# Revit family: Strangregulierventil mit Messblende für Trinkwasseranlagen 4017 MW
name_source: partatom
category: Rohrzubehör
units: mm (PartAtom-declared; Revit-internal decimal feet)

## family parameters
Arbeitsebenenbasiert = Nein
Beim Laden mit Abzugskörper schneiden = Nein
Bemaßung runder Anschluss = Durchmesser verwenden
Gemeinsam genutzt = Nein
Immer vertikal = Ja
OmniClass-Nummer = 23.65.55.14
OmniClass-Titel = Valves for Liquid Services
Teiletyp = Unterbricht

## types (1)
- Strangregulierventil mit Messblende für Trinkwasseranlagen 4017 MW
    Anwendungsgebiet = Zum Absperren und Regulieren von Trinkwasseranlagen in Gebäuden bzw. zum hydraulischen Abgleich von Versorgungsleitungen.
    Ausführung = Nach Norm BS 7350 PN20 Serie B
Schrägsitzregulierventil aus Kupferlegierung.
Alle wasserberührten Metallteile sind aus entzinkungsbeständiger Kupferlegierung hergestellt.
Die Oberteile sind mit nichtsteigender Spindel ausgestattet.
    E00 = 0 mm  [stored 0 ft]
    Gehäuse = entzinkungsbeständiges Messing (DZR)
    H02 = 13 mm
    Handrad = Kunststoff, grün
    Hersteller = HERZ Armaturen Ges.m.b.H.
    Hinweis = Gemäß Art 33 der REACH-Verordnung (EG Nr. 1907/2006) sind wir verpflichtet, darauf hinzuweisen, dass der Stoff Blei auf der SVHC-Liste geführt wird und dass alle aus Messing bestehenden Bauteile, die in unseren Erzeugnissen verarbeitet sind, mehr als 0,1 % (w/w) Blei (CAS: 7439-92-1 / EINECS: 231-100-4) enthalten.
Da Blei als Legierungsbestandteil fest gebunden ist, sind keine Expositionen zu erwarten und daher sind keine zusätzlichen Angaben zur sicheren Verwendung notwendig.
    Max. Betriebsdruck bei 20°C = 2000000.0 Pa
    Max. Betriebstemperatur bei 10 bar = 85 °C
    Max. Differenzdruck bei geschlossenen Sitz = 1000000.0 Pa
    Medium = Trinkwasser
    O-Ringe = EPDM
    R01 = 12 mm  [stored 0.0393701 ft]
    R02 = 9.5 mm  [stored 0.031168 ft]
    R03 = 21.5 mm
    S03 = 60 mm  [stored 0.19685 ft]
    SCRNCODE = 04;00;02
    SCRNSEQ = FW;SBT_TYP_FW="109";2
    SW01 = 60.00°
    URL = www.herz-armaturen.at
    Vorgabe-Ansicht = 0 mm  [stored 0 ft]
    W01 = 45.00°

note: [stored X ft] marks values corroborated as IEEE doubles in the binary element streams (Revit-internal decimal feet)
